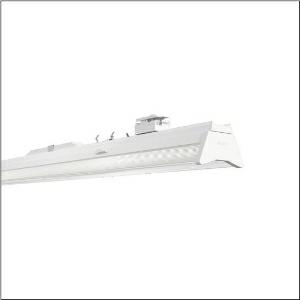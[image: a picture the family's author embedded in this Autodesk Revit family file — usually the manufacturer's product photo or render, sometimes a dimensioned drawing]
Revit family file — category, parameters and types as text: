
# Revit family: licross_r__21_performance_mo_52td16cn46xg_4d89
name_source: partatom
category: Lighting Fixtures
units: mm (PartAtom-declared; Revit-internal decimal feet)

## family parameters
Cut with Voids When Loaded = No
Host = Face
Light Source = No
Part Type = Normal
Room Calculation Point = No
Round Connector Dimension = Use Diameter
Shared = No

## types (1)
- --- (1 x LED, 6000 lm, 32 W, 4000K)
    Apparent Load = 32 VA
    CIE Flux Codes = 66 88 96 79 100
    Color Rendering = 80
    Color Temperature = 4000K
    Default Elevation = 1800 mm
    Description = Licross® 21 Performance MO, luminaire insert, of sheet steel, galvanised, coil coated, white, length: 1.500mm, width: 120mm, height: 123mm, LED rated luminous flux: 6.000lm, light colour: 840, control gear: ON/OFF Multilumen, CLOi, control gear: ECG Multilumen, with plug, 3-pole, with phase selection, mains connection: 220..240V, AC, 50/60Hz, start of lifetime: 32W, end of service life: 38W, internal wiring halogen-free, primary light control with lens, of plastic, primary optical cover: cover, of PMMA, light emission: direct/indirect distribution, primary light characteristic: symmetric, protection rating (complete): IP54, insulation class (complete): insulation class I (protective earthing), certification: CE, ENEC, UKCA, protection symbol: D if used in an environment with non-conductive dust loads with corresponding accessories, impact resistance: IK06, permissible ambient temperature for indoor applications: -35..+55°C, corresponds to IFS (International Featured Standards) requirements for safety and quality in the food industry, reducing of maximum allowable ambient temperature of 5°C with ceiling mounting, LABS conformity tested according to VDMA 24364:2018-05, packaging unit: 1 piece
    Height = 114 mm
    Lamp = 1 x LED
    Lamp Light Flux = 6000 lm
    Lamp Power = 32 W
    Lamp count = 1
    Length = 1500 mm
    Luminous efficacy = 188 lm/W
    Manufacturer = Siteco
    ModVariant = No
    Model = 52TD16CN46XG
    Mounting Place = Ceiling
    Mounting Type = Pendant
    Number of Poles = 1
    OnlyDefault = Yes
    Power Factor = 1
    Product Name = Licross® 21 Performance MO
    Product group = luminaire insert | ceiling pendant
    ProductGroupID = 902
    Protection Class = Protection class I
    Protection Degree = IP 54
    RLX_Detail_Level = 1
    RLX_Emergency_Light_Flux = 0 lm
    RLX_Emergency_Type = 0
    RLX_Emergency_Type_DB = No
    RlxData = <blob elided: 31813 chars, md5=009d7a23>
    Socket = socket
    Standby Power = 0 W
    System Light Flux = 6000 lm
    System Power = 32 W
    Type Comments = factory setting: luminous flux: 100 % | (A | C | E) | 74 mA
    Type Image = l_1256138.jpg
    URL = http://relux.com
    VarID = @adj_133027
    Voltage = 0 V
    Weight = 0.00 kg
    Width = 120 mm

## geometry (parser evidence)
native form markers: Blend x4, Sweep x13
no freeform markers — native parametric forms only
